# Revit family: Building-IEC309Connections-GEWISS-IEC309HP-STRAIGHT_FLUSH_MOUNT_INLET_32A_IP67
name_source: partatom
category: Apparecchi elettrici
units: mm (PartAtom-declared; Revit-internal decimal feet)

## family parameters
Condiviso = No
Host = Superficie
Mantenere orientamento annotazione = Sì
Punto di calcolo locali = Sì
Quota connettore circolare = Usa diametro
Taglio con vuoti quando caricato = No
Tipo di parte = Normale

## types (12) — shared parameters
BLOCCO = B=C
Breaking capacity at 1.1 Un = 40A
Catalogue = BUILDING
Corpo centrale = Default(2)
Electrocod = 2230
FORMULA = 1000 mm  [stored 3.28084 ft]
Flange dimensions (mm) = 95x80
Frequency = 50/60 Hz
Glow wire test: = 850 °C (active parts) - 650 °C (passive parts)
IDF = f4ffd64b-f466-47c0-b082-9e97be64ef99
IDT = 52ef395f395f4125bd0a3cd8d910fdee
IP degree = IP67
Immagine tipo = <Nessuno>
Insulation resistance = - 10 M?
L = 155 mm
Operating temperature: = -25 +55 °C
Permissible overload = 42A
Piastra = Default(2)
Produttore = GEWISS S.p.A.
Prospetto di default = 1219 mm
Rated current (A) = 32
SEO = Inlet
SPinotto = Default(2)
Shock resistance = IK08
Spostamento_S = 960 mm
Technical sheet = https://www.gewiss.com
Terminal tightening capacity = 2.5-6mm² flexible cables - 2.5-10mm² rigid cables
Thermo-pressure with ball = 125 °C (active parts) - 80 °C (passive parts)
Total number of operations = -2000
Type of wiring = With screw
Typology = Straight flush mounting inlet
URL = https://www.gewiss.com
Version file RFA = 21.11
W = 115 mm

## per-type parameters (varying)
| type | Colour: | Descrizione | Modello | No. of poles | Rated voltage | Reference h |
| GW60241 - IP67 APPL.INLET 3P+E 32A 400V 6H | Red | IP67 APPL.INLET 3P+E 32A 400V 6H | GW60241 | 3P+E | 380-415V | 6 |
| GW60238 - IP67 APPL.INLET 3P+E 32A 230V 9H | Blue | IP67 APPL.INLET 3P+E 32A 230V 9H | GW60238 | 3P+E | 200-250V | 9 |
| GW60239 - IP67 APPL.INLET 3P+N+E 32A 230V 9H | Blue | IP67 APPL.INLET 3P+N+E 32A 230V 9H | GW60239 | 3P+N+E | 200-250V | 9 |
| GW60268 - IP67 APPL.INLET 3P+E 32A 380V 3H | Red | IP67 APPL.INLET 3P+E 32A 380V 3H | GW60268 | 3P+E | 380-440V | 3 |
| GW60244 - IP67 APPL.INLET 3P+N+E 32A 500V 7H | Black | IP67 APPL.INLET 3P+N+E 32A 500V 7H | GW60244 | 3P+N+E | 480-500V | 7 |
| GW60243 - IP67 APPL.INLET 3P+E 32A 500V 7H | Black | IP67 APPL.INLET 3P+E 32A 500V 7H | GW60243 | 3P+E | 480-500V | 7 |
| GW60235 - IP67 APPL.INLET 3P+E 32A 110V 4H | Yellow | IP67 APPL.INLET 3P+E 32A 110V 4H | GW60235 | 3P+E | 100-130V | 4 |
| GW60237 - IP67 APPL.INLET 2P+E 32A 230V 6H | Blue | IP67 APPL.INLET 2P+E 32A 230V 6H | GW60237 | 2P+E | 200-250V | 6 |
| GW60240 - IP67 APPL.INLET 2P+E 32A 400V 9H | Red | IP67 APPL.INLET 2P+E 32A 400V 9H | GW60240 | 2P+E | 380-415V | 9 |
| GW60242 - IP67 APPL.INLET 3P+N+E 32A 400V 6H | Red | IP67 APPL.INLET 3P+N+E 32A 400V 6H | GW60242 | 3P+N+E | 380-415V | 6 |
| GW60236 - IP67 APPL.INLET 3P+N+E 32A 110V 4H | Yellow | IP67 APPL.INLET 3P+N+E 32A 110V 4H | GW60236 | 3P+N+E | 100-130V | 4 |
| GW60234 - IP67 APPL.INLET 2P+E 32A 110V 4H | Yellow | IP67 APPL.INLET 2P+E 32A 110V 4H | GW60234 | 2P+E | 100-130V | 4 |

note: [stored X ft] marks values corroborated as IEEE doubles in the binary element streams (Revit-internal decimal feet)

## geometry (parser evidence)
native form markers: Sweep x2
no freeform markers — native parametric forms only
